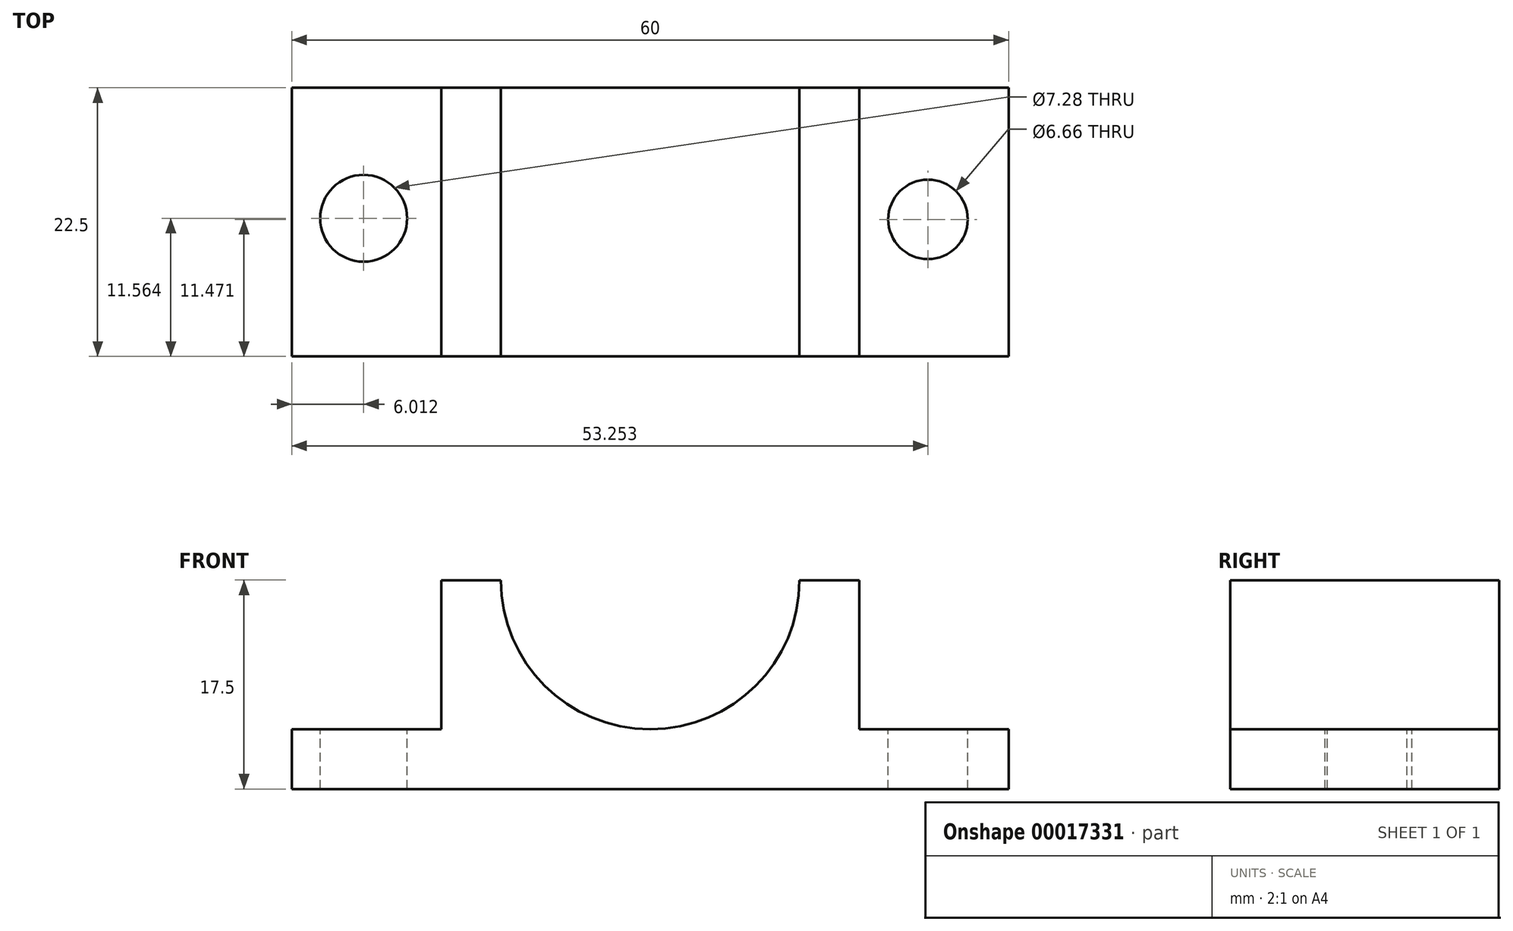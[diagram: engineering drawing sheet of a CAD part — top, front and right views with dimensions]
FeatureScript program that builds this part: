
annotation { "Feature Type Name" : "Feature", "Feature Type Description" : "" }
export const myFeature = defineFeature(function(context is Context, id is Id, definition is map)
    precondition{}
    {
        {
            var Q0;
            Q0=qCreatedBy(makeId("Front.planeOp"),FACE);
            var sketch = newSketch(context, id + "F0", { "sketchPlane" : qUnion([Q0])});
            skLineSegment(sketch, "E0", {"start": v(-21.32, -4.1) * mm, "end": v(38.68, -4.1) * mm});
            skLineSegment(sketch, "E1", {"start": v(38.68, -4.1) * mm, "end": v(38.68, 0.9) * mm});
            skLineSegment(sketch, "E2", {"start": v(38.68, 0.9) * mm, "end": v(26.18, 0.9) * mm});
            skLineSegment(sketch, "E3", {"start": v(26.18, 0.9) * mm, "end": v(26.18, 13.4) * mm});
            skLineSegment(sketch, "E4", {"start": v(-8.82, 13.4) * mm, "end": v(-8.82, 0.9) * mm});
            skLineSegment(sketch, "E5", {"start": v(-8.82, 0.9) * mm, "end": v(-21.32, 0.9) * mm});
            skLineSegment(sketch, "E6", {"start": v(-21.32, 0.9) * mm, "end": v(-21.32, -4.1) * mm});
            skArc(sketch, "E7", {"start": v(-3.82, 13.4) * mm, "mid": v(8.68, 0.9) * mm, "end": v(21.18, 13.4) * mm});
            skLineSegment(sketch, "E8", {"start": v(-8.82, 13.4) * mm, "end": v(-3.82, 13.4) * mm});
            skLineSegment(sketch, "E9", {"start": v(21.18, 13.4) * mm, "end": v(26.18, 13.4) * mm});
            skSolve(sketch);
        }
        {
            var Q0;
            Q0=makeQuery(id+"F0.imprint","IMPRINT",FACE,{"disambiguationData":[TD([[makeQuery(id+"F0.imprint","IMPRINT",EDGE,{"derivedFrom":sQuery(id+"F0.wireOp",EDGE,"E0")}),1.0]])]});
            extrude(context, id + "F1", {"entities" : qUnion([Q0]), "depth" : 22.5 * mm});
        }
        {
            var Q0;
            Q0=makeQuery(id+"F1.opExtrude","SWEPT_FACE",FACE,{"disambiguationData":[OSD([sQuery(id+"F0.wireOp",EDGE,"E5")])]});
            var sketch = newSketch(context, id + "F2", { "sketchPlane" : qUnion([Q0])});
            skCircle(sketch, "E10", {"center": v(-15.3, -10.94) * mm, "radius": 3.64 * mm});
            skCircle(sketch, "E11", {"center": v(31.93, -10.94) * mm, "radius": 3.44 * mm});
            skSolve(sketch);
        }
        {
            var Q0;
            Q0=makeQuery(id+"F1.opExtrude","SWEPT_FACE",FACE,{"disambiguationData":[OSD([sQuery(id+"F0.wireOp",EDGE,"E2")])]});
            var sketch = newSketch(context, id + "F3", { "sketchPlane" : qUnion([Q0])});
            skCircle(sketch, "E12", {"center": v(31.93, -11.03) * mm, "radius": 3.33 * mm});
            skSolve(sketch);
        }
        {
            var Q0;
            Q0=makeQuery(id+"F2.imprint","IMPRINT",FACE,{"disambiguationData":[TD([[makeQuery(id+"F2.imprint","IMPRINT",EDGE,{"derivedFrom":sQuery(id+"F2.wireOp",EDGE,"E10")}),1.0]])]});
            extrude(context, id + "F4", {"entities" : qUnion([Q0]), "operationType" : NewBodyOperationType.REMOVE, "oppositeDirection" : true, "depth" : 25 * mm});
        }
        {
            var Q0;
            Q0=makeQuery(id+"F3.imprint","IMPRINT",FACE,{"disambiguationData":[TD([[makeQuery(id+"F3.imprint","IMPRINT",EDGE,{"derivedFrom":sQuery(id+"F3.wireOp",EDGE,"E12")}),1.0]])]});
            extrude(context, id + "F5", {"entities" : qUnion([Q0]), "operationType" : NewBodyOperationType.REMOVE, "oppositeDirection" : true, "depth" : 25 * mm});
        }
    });
